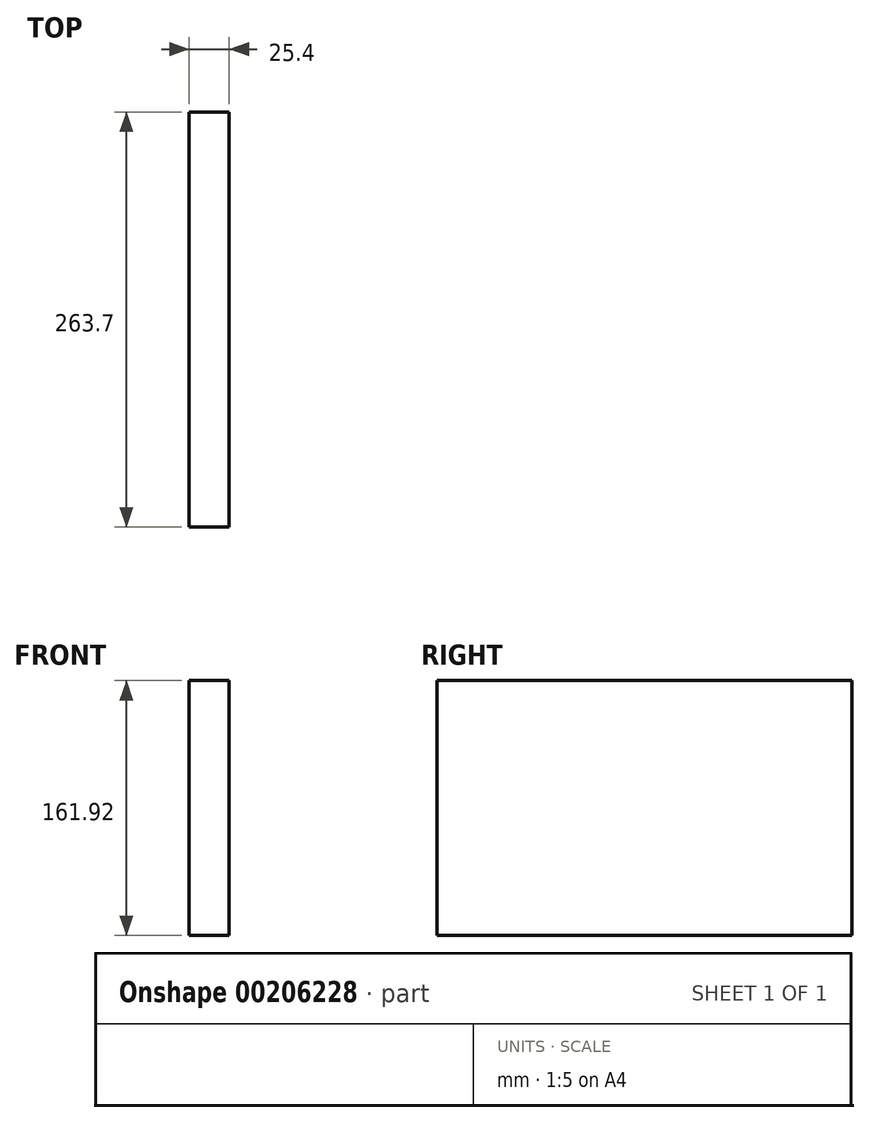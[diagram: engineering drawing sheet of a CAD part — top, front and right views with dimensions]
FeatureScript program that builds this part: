
annotation { "Feature Type Name" : "Feature", "Feature Type Description" : "" }
export const myFeature = defineFeature(function(context is Context, id is Id, definition is map)
    precondition{}
    {
        {
            var Q0;
            Q0=qCreatedBy(makeId("Right.planeOp"),FACE);
            var sketch = newSketch(context, id + "F0", { "sketchPlane" : qUnion([Q0])});
            skLineSegment(sketch, "E0.bottom", {"start": v(-131.85, -80.96) * mm, "end": v(131.85, -80.96) * mm});
            skLineSegment(sketch, "E0.top", {"start": v(-131.85, 80.96) * mm, "end": v(131.85, 80.96) * mm});
            skLineSegment(sketch, "E0.left", {"start": v(-131.85, -80.96) * mm, "end": v(-131.85, 80.96) * mm});
            skLineSegment(sketch, "E0.right", {"start": v(131.85, -80.96) * mm, "end": v(131.85, 80.96) * mm});
            skPoint(sketch, "E0.middle", {"position": v(0, 0) * mm});
            skSolve(sketch);
        }
        {
            var Q0;
            Q0 = qSketchRegion(id + "F0", true);
            extrude(context, id + "F1", {"entities" : qUnion([Q0]), "depth" : 25.4 * mm});
        }
    });
